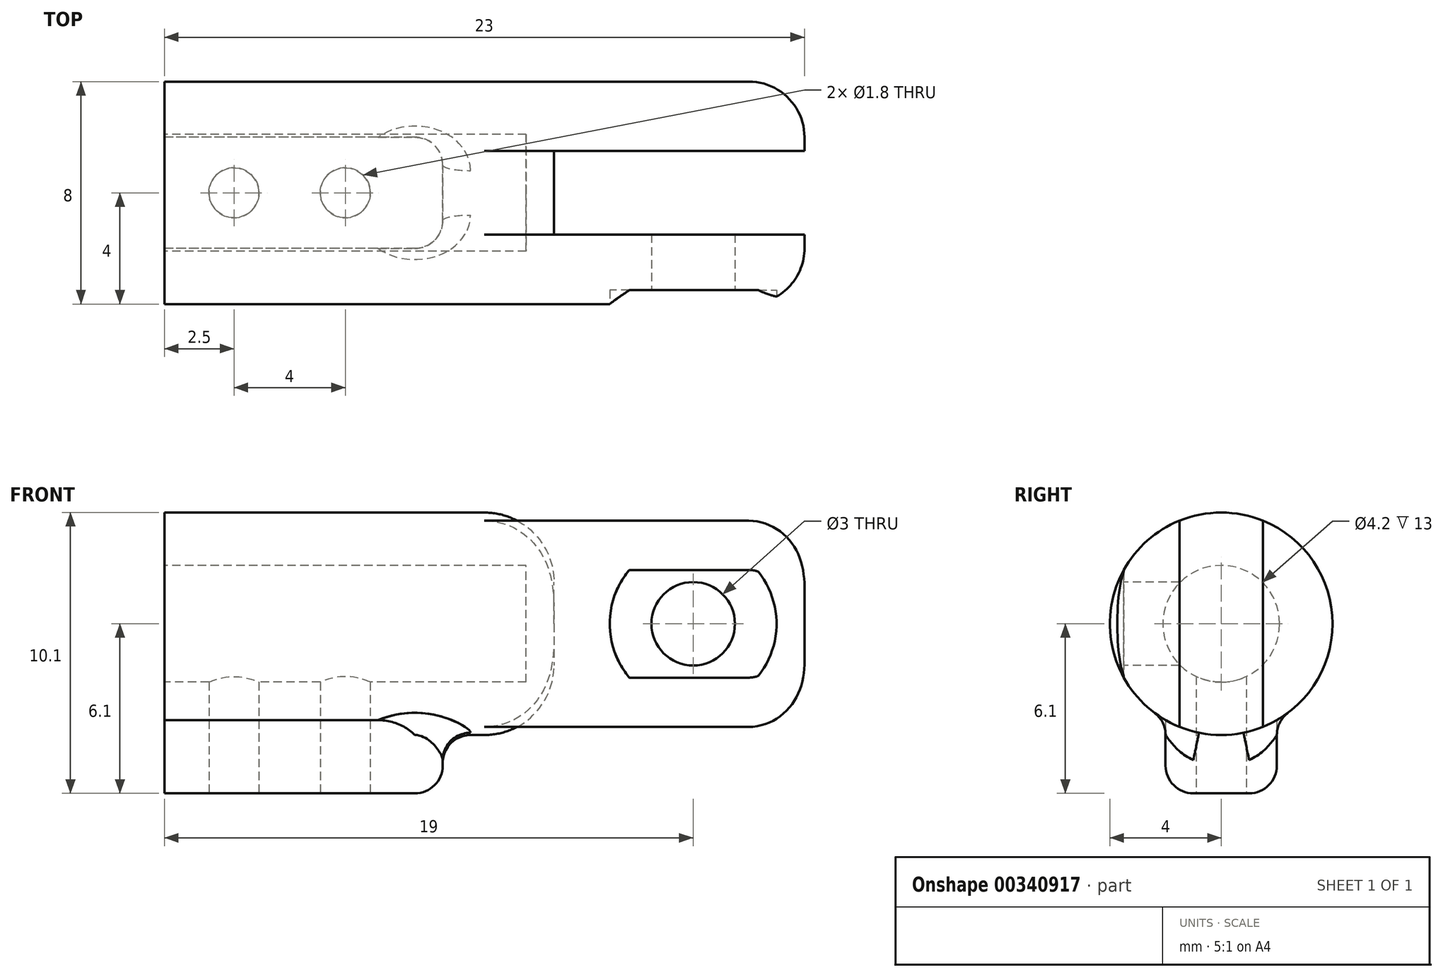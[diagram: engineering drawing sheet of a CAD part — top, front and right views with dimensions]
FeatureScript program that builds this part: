
annotation { "Feature Type Name" : "Feature", "Feature Type Description" : "" }
export const myFeature = defineFeature(function(context is Context, id is Id, definition is map)
    precondition{}
    {
        {
            var Q0;
            Q0=qCreatedBy(makeId("Right.planeOp"),FACE);
            var sketch = newSketch(context, id + "F0", { "sketchPlane" : qUnion([Q0])});
            skCircle(sketch, "E0", {"center": v(0, 0) * mm, "radius": 2.1 * mm});
            skCircle(sketch, "E1", {"center": v(0, 0) * mm, "radius": 4 * mm});
            skLineSegment(sketch, "E2", {"start": v(2, -3.46) * mm, "end": v(2, -6.1) * mm});
            skLineSegment(sketch, "E3", {"start": v(2, -6.1) * mm, "end": v(-2, -6.1) * mm});
            skLineSegment(sketch, "E4", {"start": v(-2, -6.1) * mm, "end": v(-2, -3.46) * mm});
            skSolve(sketch);
        }
        {
            var Q0;
            Q0=makeQuery(id+"F0.imprint","IMPRINT",FACE,{"disambiguationData":[TD([[makeQuery(id+"F0.imprint","IMPRINT",EDGE,{"derivedFrom":sQuery(id+"F0.wireOp",EDGE,"E0")}),-1.0]])]});
            var Q1;
            Q1=makeQuery(id+"F0.imprint","IMPRINT",FACE,{"disambiguationData":[TD([[makeQuery(id+"F0.imprint","IMPRINT",EDGE,{"derivedFrom":sQuery(id+"F0.wireOp",EDGE,"E0")}),1.0]])]});
            extrude(context, id + "F1", {"entities" : qUnion([Q0, Q1]), "depth" : 23 * mm, "offsetDistance" : 25 * mm});
        }
        {
            var Q0;
            Q0=makeQuery(id+"F0.imprint","IMPRINT",FACE,{"disambiguationData":[TD([[makeQuery(id+"F0.imprint","IMPRINT",EDGE,{"derivedFrom":sQuery(id+"F0.wireOp",EDGE,"E0")}),1.0]])]});
            extrude(context, id + "F2", {"entities" : qUnion([Q0]), "operationType" : NewBodyOperationType.REMOVE, "depth" : 13 * mm, "offsetDistance" : 25 * mm});
        }
        {
            var Q0;
            Q0=makeQuery(id+"F1.opExtrude","CAP_FACE",FACE,{"disambiguationData":[OSD([sQuery(id+"F0.wireOp",EDGE,"E0"),sQuery(id+"F0.wireOp",EDGE,"E1")])],"isStart":false});
            cPlane(context, id + "F3", {"entities" : qUnion([Q0]), "cplaneType" : CPlaneType.OFFSET, "offset" : 0 * mm, "width" : 150 * mm, "height" : 150 * mm});
        }
        {
            var Q0;
            Q0=qCreatedBy(id+"F3.planeOp",FACE);
            var sketch = newSketch(context, id + "F4", { "sketchPlane" : qUnion([Q0])});
            skLineSegment(sketch, "E5.bottom", {"start": v(1.5, -4) * mm, "end": v(-1.5, -4) * mm});
            skLineSegment(sketch, "E5.top", {"start": v(1.5, 4) * mm, "end": v(-1.5, 4) * mm});
            skLineSegment(sketch, "E5.left", {"start": v(1.5, -4) * mm, "end": v(1.5, 4) * mm});
            skLineSegment(sketch, "E5.right", {"start": v(-1.5, -4) * mm, "end": v(-1.5, 4) * mm});
            skPoint(sketch, "E5.middle", {"position": v(0, 0) * mm});
            skSolve(sketch);
        }
        {
            var Q0;
            {var subQ0=sQuery(id+"F4.wireOp",EDGE,"E5.left");var subQ1=sQuery(id+"F6oWoKsDEnx1sjk_1.wireOp",EDGE,"171556a4-600e-4862-a10e-88d223d029910.MirrorCS");var subQ2=sQuery(id+"F6oWoKsDEnx1sjk_1.wireOp",EDGE,"nGa1sqjB-H7Ow-3scy-iZwB-qixYv0Jmrafc.right");var subQ3=makeQuery(id+"FhGqZDnQz9BZsxH_1.opLoft","MID_CAP_EDGE",EDGE,{"disambiguationData":[OSD([subQ2,subQ1,sQuery(id+"F6oWoKsDEnx1sjk_1.wireOp",EDGE,"QtEZCRTN-AAdx-a9Je-NfUg-qH4uqyxohC3w")])],"capPos":1.0});var subQ4=makeQuery(id+"F4.imprint","INTERSECT",VERTEX,{"derivedFrom":[subQ3,subQ0]});Q0=makeQuery(id+"F4.imprint","IMPRINT",FACE,{"disambiguationData":[TD([[makeQuery(id+"F4.imprint","IMPRINT",EDGE,{"disambiguationData":[TD([[subQ4,-1.0]])],"derivedFrom":subQ0}),1.0]])]});}
            var Q1;
            {var subQ0=sQuery(id+"F4.wireOp",EDGE,"E5.top");Q1=makeQuery(id+"F4.imprint","IMPRINT",FACE,{"disambiguationData":[TD([[makeQuery(id+"F4.imprint","IMPRINT",EDGE,{"derivedFrom":subQ0}),1.0]])]});}
            var Q2;
            {var subQ0=sQuery(id+"F4.wireOp",EDGE,"E5.bottom");Q2=makeQuery(id+"F4.imprint","IMPRINT",FACE,{"disambiguationData":[TD([[makeQuery(id+"F4.imprint","IMPRINT",EDGE,{"derivedFrom":subQ0}),-1.0]])]});}
            extrude(context, id + "F5", {"entities" : qUnion([Q0, Q1, Q2]), "operationType" : NewBodyOperationType.REMOVE, "oppositeDirection" : true, "depth" : 9 * mm, "offsetDistance" : 25 * mm});
        }
        {
            var Q0;
            {var subQ0=sQuery(id+"F0.wireOp",EDGE,"E1");Q0=makeQuery(id+"F5.boolean.opBoolean","SPLIT",EDGE,{"disambiguationData":[TD([makeQuery(id+"F5.opExtrude","SWEPT_FACE",FACE,{"disambiguationData":[OSD([sQuery(id+"F4.wireOp",EDGE,"E5.right")])]})])],"derivedFrom":makeQuery(id+"F1.opExtrude","CAP_EDGE",EDGE,{"disambiguationData":[OSD([subQ0])],"isStart":false})});}
            cPoint(context, id + "F6", {"entities" : qUnion([Q0]), "parameter" : 0.5});
        }
        {
            var Q0;
            Q0=qCreatedBy(makeId("Front.planeOp"),FACE);
            var Q1;
            Q1 = qCreatedBy(id + "F6" ,VERTEX);
            cPlane(context, id + "F7", {"entities" : qUnion([Q0, Q1]), "cplaneType" : CPlaneType.PLANE_POINT, "offset" : 10 * mm, "width" : 150 * mm, "height" : 150 * mm});
        }
        {
            var Q0;
            Q0=qCreatedBy(id+"F7.planeOp",FACE);
            var sketch = newSketch(context, id + "F8", { "sketchPlane" : qUnion([Q0])});
            skPoint(sketch, "E6", {"position": v(19, 0) * mm});
            skSolve(sketch);
        }
        {
            var Q0;
            Q0=sQuery(id+"F8.wireOp",VERTEX,"E6");
            var Q1;
            Q1=makeQuery(id+"F1.opExtrude","SWEPT_BODY",BODY,{"disambiguationData":[OSD([sQuery(id+"F0.wireOp",EDGE,"E1")])]});
            hole(context, id + "F9", {"style" : HoleStyle.C_BORE, "endStyle" : HoleEndStyle.BLIND, "holeDiameter" : 3 * mm, "cBoreDiameter" : 6 * mm, "cBoreDepth" : 0.5 * mm, "majorDiameter" : 5 * mm, "holeDepth" : 3 * mm, "isTappedThrough" : true, "tappedDepth" : 12 * mm, "tapClearance" : 3, "startFromSketch" : true, "locations" : qUnion([Q0]), "scope" : qUnion([Q1])});
        }
        {
            var Q0;
            Q0=makeQuery(id+"F5.boolean.opBoolean","INTERSECT",EDGE,{"disambiguationData":[OD(0.0)],"derivedFrom":[makeQuery(id+"F1.opExtrude","SWEPT_FACE",FACE,{"disambiguationData":[OSD([sQuery(id+"F0.wireOp",EDGE,"E1")])]}),makeQuery(id+"F5.opExtrude","CAP_FACE",FACE,{"disambiguationData":[OSD([sQuery(id+"F4.wireOp",EDGE,"E5.bottom"),sQuery(id+"F4.wireOp",EDGE,"E5.top"),sQuery(id+"F4.wireOp",EDGE,"E5.left"),sQuery(id+"F4.wireOp",EDGE,"E5.right")])],"isStart":false})]});
            var Q1;
            Q1=makeQuery(id+"F5.boolean.opBoolean","INTERSECT",EDGE,{"disambiguationData":[OD(1.0)],"derivedFrom":[makeQuery(id+"F1.opExtrude","SWEPT_FACE",FACE,{"disambiguationData":[OSD([sQuery(id+"F0.wireOp",EDGE,"E1")])]}),makeQuery(id+"F5.opExtrude","CAP_FACE",FACE,{"disambiguationData":[OSD([sQuery(id+"F4.wireOp",EDGE,"E5.bottom"),sQuery(id+"F4.wireOp",EDGE,"E5.top"),sQuery(id+"F4.wireOp",EDGE,"E5.left"),sQuery(id+"F4.wireOp",EDGE,"E5.right")])],"isStart":false})]});
            fillet(context, id + "F10", {"entities" : qUnion([Q0, Q1]), "radius" : 2.5 * mm, "tangentPropagation" : true, "allowEdgeOverflow" : false});
        }
        {
            var Q0;
            {var subQ0=sQuery(id+"F0.wireOp",EDGE,"E1");Q0=makeQuery(id+"F5.boolean.opBoolean","SPLIT",EDGE,{"disambiguationData":[TD([makeQuery(id+"F5.opExtrude","SWEPT_FACE",FACE,{"disambiguationData":[OSD([sQuery(id+"F4.wireOp",EDGE,"E5.left")])]})])],"derivedFrom":makeQuery(id+"F1.opExtrude","CAP_EDGE",EDGE,{"disambiguationData":[OSD([subQ0])],"isStart":false})});}
            var Q1;
            {var subQ0=sQuery(id+"F0.wireOp",EDGE,"E1");Q1=makeQuery(id+"F5.boolean.opBoolean","SPLIT",EDGE,{"disambiguationData":[TD([makeQuery(id+"F5.opExtrude","SWEPT_FACE",FACE,{"disambiguationData":[OSD([sQuery(id+"F4.wireOp",EDGE,"E5.right")])]})])],"derivedFrom":makeQuery(id+"F1.opExtrude","CAP_EDGE",EDGE,{"disambiguationData":[OSD([subQ0])],"isStart":false})});}
            fillet(context, id + "F11", {"entities" : qUnion([Q0, Q1]), "radius" : 2 * mm, "tangentPropagation" : true, "allowEdgeOverflow" : false});
        }
        {
            var Q0;
            {var subQ0=sQuery(id+"F0.wireOp",EDGE,"E2");Q0=makeQuery(id+"F0.imprint","IMPRINT",FACE,{"disambiguationData":[TD([[makeQuery(id+"F0.imprint","IMPRINT",EDGE,{"derivedFrom":subQ0}),-1.0]])]});}
            extrude(context, id + "F12", {"entities" : qUnion([Q0]), "operationType" : NewBodyOperationType.ADD, "depth" : 10 * mm, "offsetDistance" : 25 * mm});
        }
        {
            var Q0;
            Q0=makeQuery(id+"F12.opExtrude","SWEPT_FACE",FACE,{"disambiguationData":[OSD([sQuery(id+"F0.wireOp",EDGE,"E3")])]});
            var sketch = newSketch(context, id + "F13", { "sketchPlane" : qUnion([Q0])});
            skPoint(sketch, "E7", {"position": v(2.5, 0) * mm});
            skPoint(sketch, "E8", {"position": v(6.5, 0) * mm});
            skSolve(sketch);
        }
        {
            var Q0;
            Q0=sQuery(id+"F13.wireOp",VERTEX,"E7");
            var Q1;
            Q1=sQuery(id+"F13.wireOp",VERTEX,"E8");
            var Q2;
            Q2=makeQuery(id+"F1.opExtrude","SWEPT_BODY",BODY,{"disambiguationData":[OSD([sQuery(id+"F0.wireOp",EDGE,"E1")])]});
            hole(context, id + "F14", {"style" : HoleStyle.SIMPLE, "endStyle" : HoleEndStyle.BLIND, "holeDiameter" : 1.8 * mm, "majorDiameter" : 5 * mm, "holeDepth" : 5 * mm, "isTappedThrough" : true, "tappedDepth" : 12 * mm, "tapClearance" : 3, "locations" : qUnion([Q0, Q1]), "scope" : qUnion([Q2])});
        }
        {
            var Q0;
            Q0=makeQuery(id+"F12.opExtrude","SWEPT_EDGE",EDGE,{"disambiguationData":[OSD([sQuery(id+"F0.wireOp",EDGE,"E3"),sQuery(id+"F0.wireOp",EDGE,"E4")])]});
            var Q1;
            Q1=makeQuery(id+"F12.opExtrude","SWEPT_EDGE",EDGE,{"disambiguationData":[OSD([sQuery(id+"F0.wireOp",EDGE,"E2"),sQuery(id+"F0.wireOp",EDGE,"E3")])]});
            var Q2;
            Q2=makeQuery(id+"F12.opExtrude","SWEPT_EDGE",EDGE,{"disambiguationData":[OSD([sQuery(id+"F0.wireOp",EDGE,"E1"),sQuery(id+"F0.wireOp",EDGE,"E4")])]});
            var Q3;
            Q3=makeQuery(id+"F12.opExtrude","SWEPT_EDGE",EDGE,{"disambiguationData":[OSD([sQuery(id+"F0.wireOp",EDGE,"E1"),sQuery(id+"F0.wireOp",EDGE,"E2")])]});
            fillet(context, id + "F15", {"entities" : qUnion([Q0, Q1, Q2, Q3]), "radius" : 1 * mm, "tangentPropagation" : true, "allowEdgeOverflow" : false});
        }
        {
            var Q0;
            Q0=makeQuery(id+"F12.opExtrude","CAP_FACE",FACE,{"disambiguationData":[OSD([sQuery(id+"F0.wireOp",EDGE,"E1"),sQuery(id+"F0.wireOp",EDGE,"E2"),sQuery(id+"F0.wireOp",EDGE,"E3"),sQuery(id+"F0.wireOp",EDGE,"E4")])],"isStart":false});
            fillet(context, id + "F16", {"entities" : qUnion([Q0]), "radius" : 1 * mm, "tangentPropagation" : true, "allowEdgeOverflow" : false});
        }
    });
